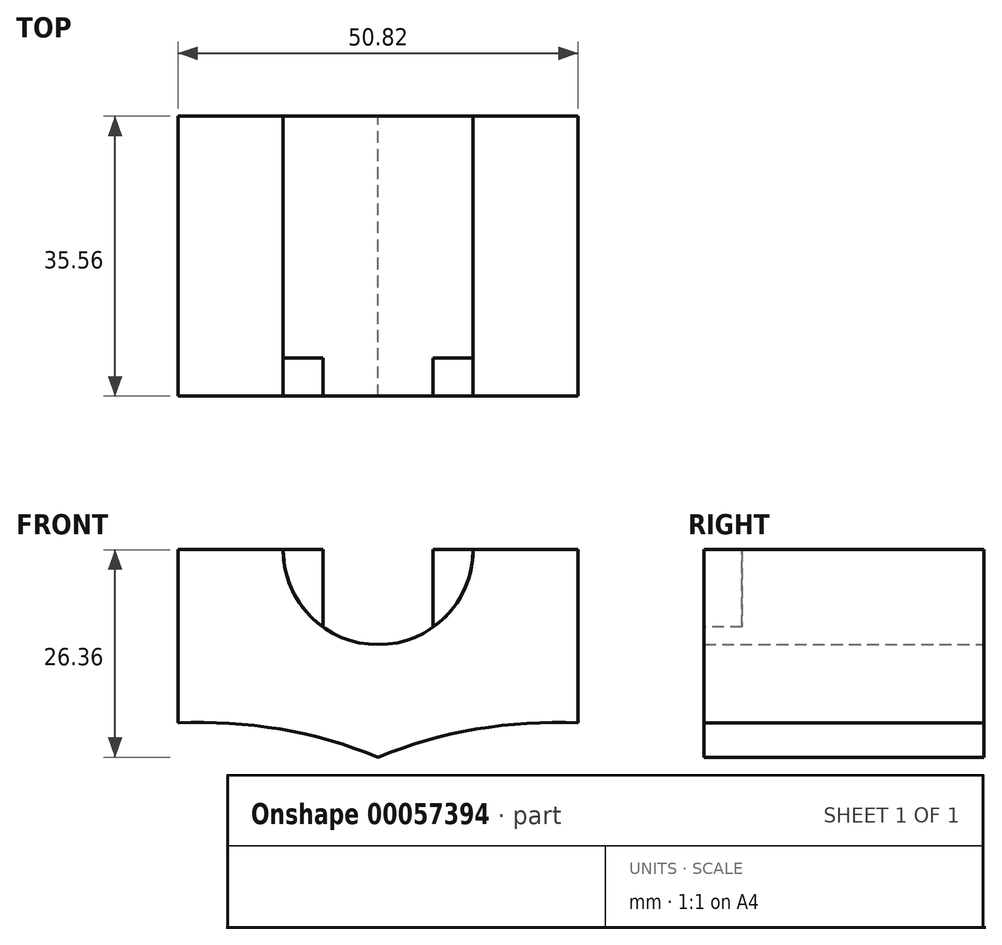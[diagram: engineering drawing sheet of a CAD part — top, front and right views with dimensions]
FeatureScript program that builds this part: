
annotation { "Feature Type Name" : "Feature", "Feature Type Description" : "" }
export const myFeature = defineFeature(function(context is Context, id is Id, definition is map)
    precondition{}
    {
        {
            var Q0;
            Q0=qCreatedBy(makeId("Front.planeOp"),FACE);
            cPlane(context, id + "F0", {"entities" : qUnion([Q0]), "cplaneType" : CPlaneType.OFFSET, "offset" : 50.8 * mm, "width" : 152.4 * mm, "height" : 152.4 * mm});
        }
        {
            var Q0;
            Q0=qCreatedBy(id+"F0.planeOp",FACE);
            cPlane(context, id + "F1", {"entities" : qUnion([Q0]), "cplaneType" : CPlaneType.OFFSET, "offset" : 50.8 * mm, "width" : 152.4 * mm, "height" : 152.4 * mm});
        }
        {
            var Q0;
            Q0=qCreatedBy(id+"F1.planeOp",FACE);
            cPlane(context, id + "F2", {"entities" : qUnion([Q0]), "cplaneType" : CPlaneType.OFFSET, "offset" : 50.8 * mm, "width" : 152.4 * mm, "height" : 152.4 * mm});
        }
        {
            var Q0;
            Q0=qCreatedBy(id+"F2.planeOp",FACE);
            cPlane(context, id + "F3", {"entities" : qUnion([Q0]), "cplaneType" : CPlaneType.OFFSET, "offset" : 50.8 * mm, "width" : 152.4 * mm, "height" : 152.4 * mm});
        }
        {
            var Q0;
            Q0=qCreatedBy(id+"F3.planeOp",FACE);
            cPlane(context, id + "F4", {"entities" : qUnion([Q0]), "cplaneType" : CPlaneType.OFFSET, "offset" : 50.8 * mm, "width" : 152.4 * mm, "height" : 152.4 * mm});
        }
        {
            var Q0;
            Q0=qCreatedBy(id+"F1.planeOp",FACE);
            var sketch = newSketch(context, id + "F5", { "sketchPlane" : qUnion([Q0])});
            skPoint(sketch, "E0.0", {"position": v(63.77, 0) * mm});
            skPoint(sketch, "E1.0", {"position": v(-63.77, 0) * mm});
            skArc(sketch, "E2", {"start": v(0, -50.8) * mm, "mid": v(-12.47, -47.23) * mm, "end": v(-25.41, -46.46) * mm});
            skArc(sketch, "E3.MirrorCS", {"start": v(0, -50.8) * mm, "mid": v(12.47, -47.23) * mm, "end": v(25.41, -46.46) * mm});
            skLineSegment(sketch, "E4", {"start": v(-25.41, -46.46) * mm, "end": v(-25.41, -24.44) * mm});
            skLineSegment(sketch, "E5", {"start": v(-25.41, -24.44) * mm, "end": v(-12.07, -24.44) * mm});
            skLineSegment(sketch, "E6", {"start": v(25.41, -46.46) * mm, "end": v(25.41, -24.44) * mm});
            skArc(sketch, "E7", {"start": v(-12.07, -24.44) * mm, "mid": v(0, -36.5) * mm, "end": v(12.07, -24.44) * mm});
            skLineSegment(sketch, "E8.trimOffspring", {"start": v(12.07, -24.44) * mm, "end": v(25.41, -24.44) * mm});
            skPoint(sketch, "E9.MirrorCS.end.orphan", {"position": v(59.44, -25.81) * mm});
            skPoint(sketch, "E10.MirrorCS.start.orphan", {"position": v(42.62, -41.1) * mm});
            skPoint(sketch, "E11.start.orphan", {"position": v(-42.62, -41.1) * mm});
            skPoint(sketch, "E12.end.orphan", {"position": v(-59.44, -25.81) * mm});
            skSolve(sketch);
        }
        {
            var Q0;
            Q0=makeQuery(id+"F5.imprint","IMPRINT",FACE,{"disambiguationData":[TD([[makeQuery(id+"F5.imprint","IMPRINT",EDGE,{"derivedFrom":sQuery(id+"F5.wireOp",EDGE,"E2")}),-1.0]])]});
            extrude(context, id + "F6", {"entities" : qUnion([Q0]), "depth" : 35.56 * mm});
        }
        {
            var Q0;
            Q0=makeQuery(id+"F6.opExtrude","CAP_FACE",FACE,{"disambiguationData":[OSD([sQuery(id+"F5.wireOp",EDGE,"E2"),sQuery(id+"F5.wireOp",EDGE,"E3.MirrorCS"),sQuery(id+"F5.wireOp",EDGE,"E4"),sQuery(id+"F5.wireOp",EDGE,"E5"),sQuery(id+"F5.wireOp",EDGE,"E6"),sQuery(id+"F5.wireOp",EDGE,"E7"),sQuery(id+"F5.wireOp",EDGE,"E8.trimOffspring")])],"isStart":false});
            var sketch = newSketch(context, id + "F7", { "sketchPlane" : qUnion([Q0])});
            skLineSegment(sketch, "E13", {"start": v(-12.07, -24.44) * mm, "end": v(-6.99, -24.44) * mm});
            skLineSegment(sketch, "E14", {"start": v(-6.99, -24.44) * mm, "end": v(-6.98, -34.28) * mm});
            skLineSegment(sketch, "E15", {"start": v(12.07, -24.44) * mm, "end": v(6.99, -24.44) * mm});
            skLineSegment(sketch, "E16", {"start": v(6.99, -24.44) * mm, "end": v(6.99, -34.28) * mm});
            skSolve(sketch);
        }
        {
            var Q0;
            {var subQ0=sQuery(id+"F7.wireOp",EDGE,"E13");Q0=makeQuery(id+"F7.imprint","IMPRINT",FACE,{"disambiguationData":[TD([[makeQuery(id+"F7.imprint","IMPRINT",EDGE,{"derivedFrom":subQ0}),-1.0]])]});}
            var Q1;
            {var subQ0=sQuery(id+"F7.wireOp",EDGE,"E15");Q1=makeQuery(id+"F7.imprint","IMPRINT",FACE,{"disambiguationData":[TD([[makeQuery(id+"F7.imprint","IMPRINT",EDGE,{"derivedFrom":subQ0}),1.0]])]});}
            extrude(context, id + "F8", {"entities" : qUnion([Q0, Q1]), "oppositeDirection" : true, "depth" : 4.83 * mm});
        }
    });
